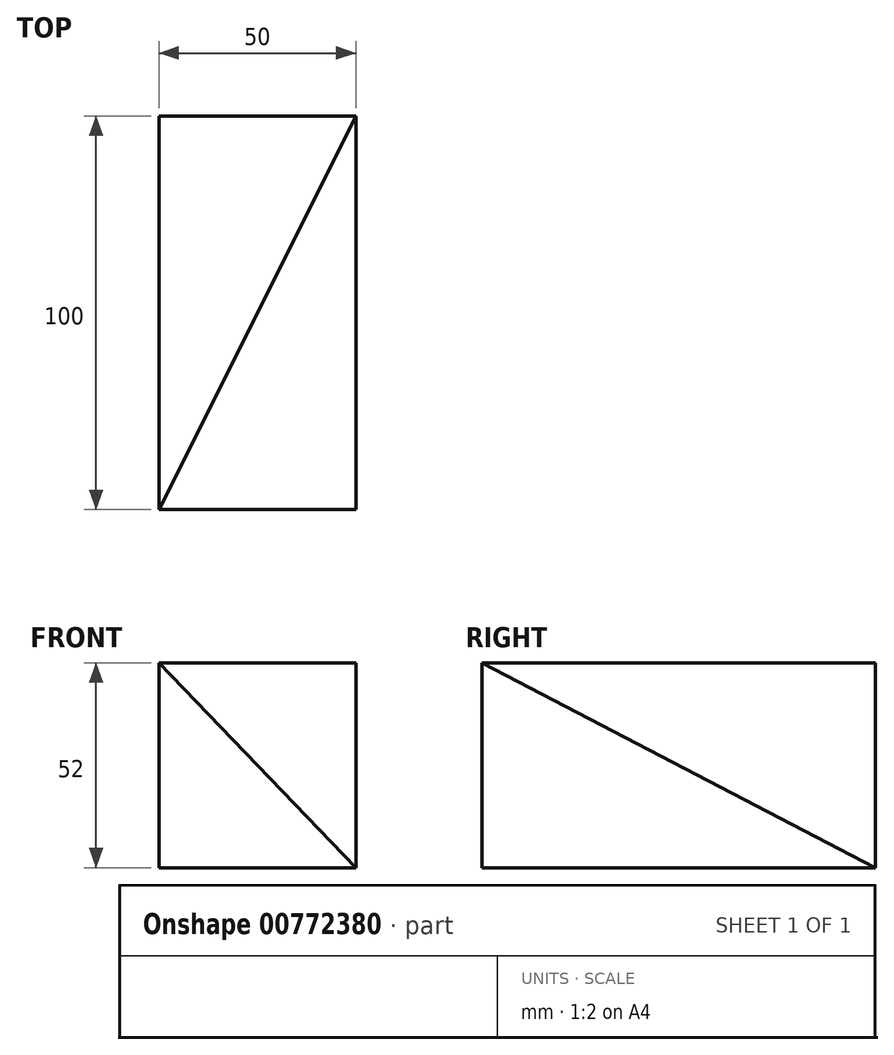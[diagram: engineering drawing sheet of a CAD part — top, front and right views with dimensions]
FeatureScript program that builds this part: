
annotation { "Feature Type Name" : "Feature", "Feature Type Description" : "" }
export const myFeature = defineFeature(function(context is Context, id is Id, definition is map)
    precondition{}
    {
        {
            var Q0;
            Q0=qCreatedBy(makeId("Top.planeOp"),FACE);
            var sketch = newSketch(context, id + "F0", { "sketchPlane" : qUnion([Q0])});
            skLineSegment(sketch, "E0", {"start": v(0, 0) * mm, "end": v(0, 100) * mm});
            skLineSegment(sketch, "E1", {"start": v(0, 100) * mm, "end": v(50, 100) * mm});
            skLineSegment(sketch, "E2", {"start": v(50, 100) * mm, "end": v(50, 0) * mm});
            skLineSegment(sketch, "E3", {"start": v(50, 0) * mm, "end": v(0, 0) * mm});
            skLineSegment(sketch, "E4", {"start": v(0, 0) * mm, "end": v(50, 100) * mm});
            skSolve(sketch);
        }
        {
            var Q0;
            Q0=makeQuery(id+"F0.imprint","IMPRINT",FACE,{"disambiguationData":[TD([[makeQuery(id+"F0.imprint","IMPRINT",EDGE,{"derivedFrom":sQuery(id+"F0.wireOp",EDGE,"E0")}),-1.0]])]});
            extrude(context, id + "F1", {"entities" : qUnion([Q0]), "depth" : 52 * mm, "offsetDistance" : 25 * mm});
        }
        {
            var Q0;
            Q0=makeQuery(id+"F1.opExtrude","SWEPT_FACE",FACE,{"disambiguationData":[OSD([sQuery(id+"F0.wireOp",EDGE,"E1")])]});
            var sketch = newSketch(context, id + "F2", { "sketchPlane" : qUnion([Q0])});
            skLineSegment(sketch, "E5", {"start": v(-50, 0) * mm, "end": v(0, 52) * mm});
            skSolve(sketch);
        }
        {
            var Q0;
            Q0=makeQuery(id+"F2.imprint","IMPRINT",FACE,{"disambiguationData":[TD([[makeQuery(id+"F2.imprint","IMPRINT",EDGE,{"derivedFrom":sQuery(id+"F2.wireOp",EDGE,"E5")}),-1.0]])]});
            var Q1;
            Q1=makeQuery(id+"F1.opExtrude","SWEPT_FACE",FACE,{"disambiguationData":[OSD([sQuery(id+"F0.wireOp",EDGE,"E4")])]});
            var Q2;
            Q2=makeQuery(id+"F1.opExtrude","CAP_VERTEX",VERTEX,{"disambiguationData":[OSD([sQuery(id+"F0.wireOp",EDGE,"E0"),sQuery(id+"F0.wireOp",EDGE,"E3"),sQuery(id+"F0.wireOp",EDGE,"E4")])],"isStart":false});
            extrude(context, id + "F3", {"entities" : qUnion([Q0]), "operationType" : NewBodyOperationType.ADD, "endBound" : BoundingType.UP_TO_VERTEX, "oppositeDirection" : true, "depth" : 25 * mm, "endBoundEntityFace" : qUnion([Q1]), "endBoundEntityVertex" : qUnion([Q2]), "offsetDistance" : 25 * mm});
        }
    });
